# Revit family: Zumtobel CROSSIGN 160 P
name_source: partatom
category: Leuchten
revit_build: Autodesk Revit 2016 (Build: 20150714_1515(x64)
units: mm (PartAtom-declared; Revit-internal decimal feet)

## family parameters
Basisbauteil = Fläche
Beim Laden mit Abzugskörper schneiden = Nein
Bemaßung runder Anschluss = Durchmesser verwenden
Gemeinsam genutzt = Nein
Lichtquelle = Ja
OmniClass-Nummer = 23.80.70.11
OmniClass-Titel = Luminaries for Internal Lighting
Raumberechnungspunkt = Nein
Teiletyp = Normal

## types (2) — shared parameters
Baugruppenkennzeichen = D5020200
Beschreibung = Escape sign LED luminaire ceiling surface-mount
Body = Zumtobel_Metal_Aluminium
Datei für fotometrisches Netz = 42180768+22168595_(STD-LEO).IES
Depth = 44 mm  [stored 0.144357 ft]
ERI = Nein
Emissionsform beim Rendern sichtbar = Nein
Farbfilter = 16777215
Farbtemperaturverschiebung bei Dämpfen der Lampe = <Keine Auswahl>
Height = 210 mm
Hersteller = Zumtobel Lighting
Lampe = LED
Modell = 42185974
Neigungswinkel = 180.00°
Scheinlast = 8 VA
URL = http://www.zumtobel.com
Voltage = 230 V
Von Breite des Rechtecks ausssenden = 44 mm  [stored 0.144357 ft]
Width = 332 mm  [stored 1.08924 ft]
zero-valued in all types: Vorgabe-Ansicht

## per-type parameters (varying)
| type | Escape Left & Right | Escape Top | Von Länge des Rechtecks aussenden |
| CROSSIGN 160 P  + O | Nein | Ja | 305 mm  [stored 1.00066 ft] |
| CROSSIGN 160 P + LR | Ja | Nein | 360 mm  [stored 1.1811 ft] |

note: [stored X ft] marks values corroborated as IEEE doubles in the binary element streams (Revit-internal decimal feet)

## geometry (parser evidence)
native form markers: Blend x6, Sweep x2
no freeform markers — native parametric forms only
